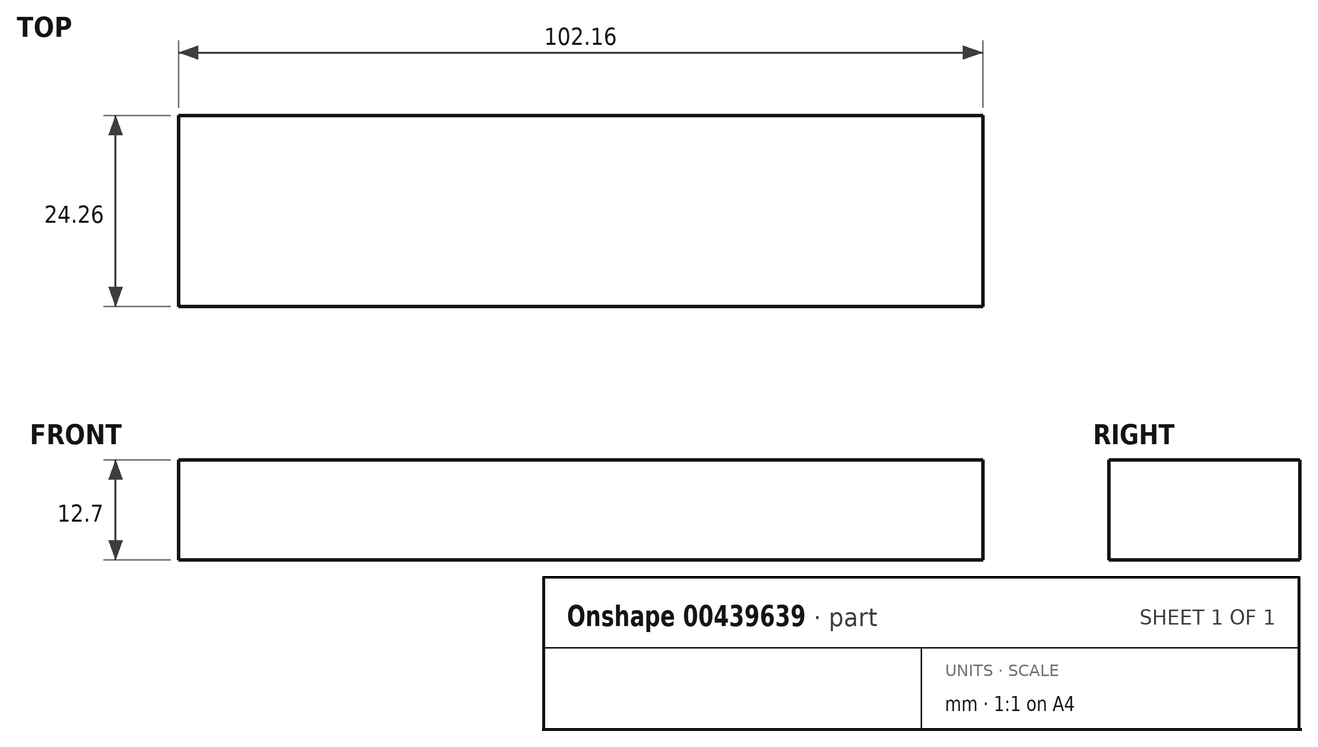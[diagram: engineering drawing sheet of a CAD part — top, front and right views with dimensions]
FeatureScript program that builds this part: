
annotation { "Feature Type Name" : "Feature", "Feature Type Description" : "" }
export const myFeature = defineFeature(function(context is Context, id is Id, definition is map)
    precondition{}
    {
        {
            var Q0;
            Q0=qCreatedBy(makeId("Top.planeOp"),FACE);
            var sketch = newSketch(context, id + "F0", { "sketchPlane" : qUnion([Q0])});
            skLineSegment(sketch, "E0.bottom", {"start": v(-63.59, 43.16) * mm, "end": v(38.57, 43.16) * mm});
            skLineSegment(sketch, "E0.top", {"start": v(-63.59, 18.9) * mm, "end": v(38.57, 18.9) * mm});
            skLineSegment(sketch, "E0.left", {"start": v(-63.59, 43.16) * mm, "end": v(-63.59, 18.9) * mm});
            skLineSegment(sketch, "E0.right", {"start": v(38.57, 43.16) * mm, "end": v(38.57, 18.9) * mm});
            skSolve(sketch);
        }
        {
            var Q0;
            Q0 = qSketchRegion(id + "F0", true);
            extrude(context, id + "F1", {"entities" : qUnion([Q0]), "depth" : 12.7 * mm});
        }
    });
